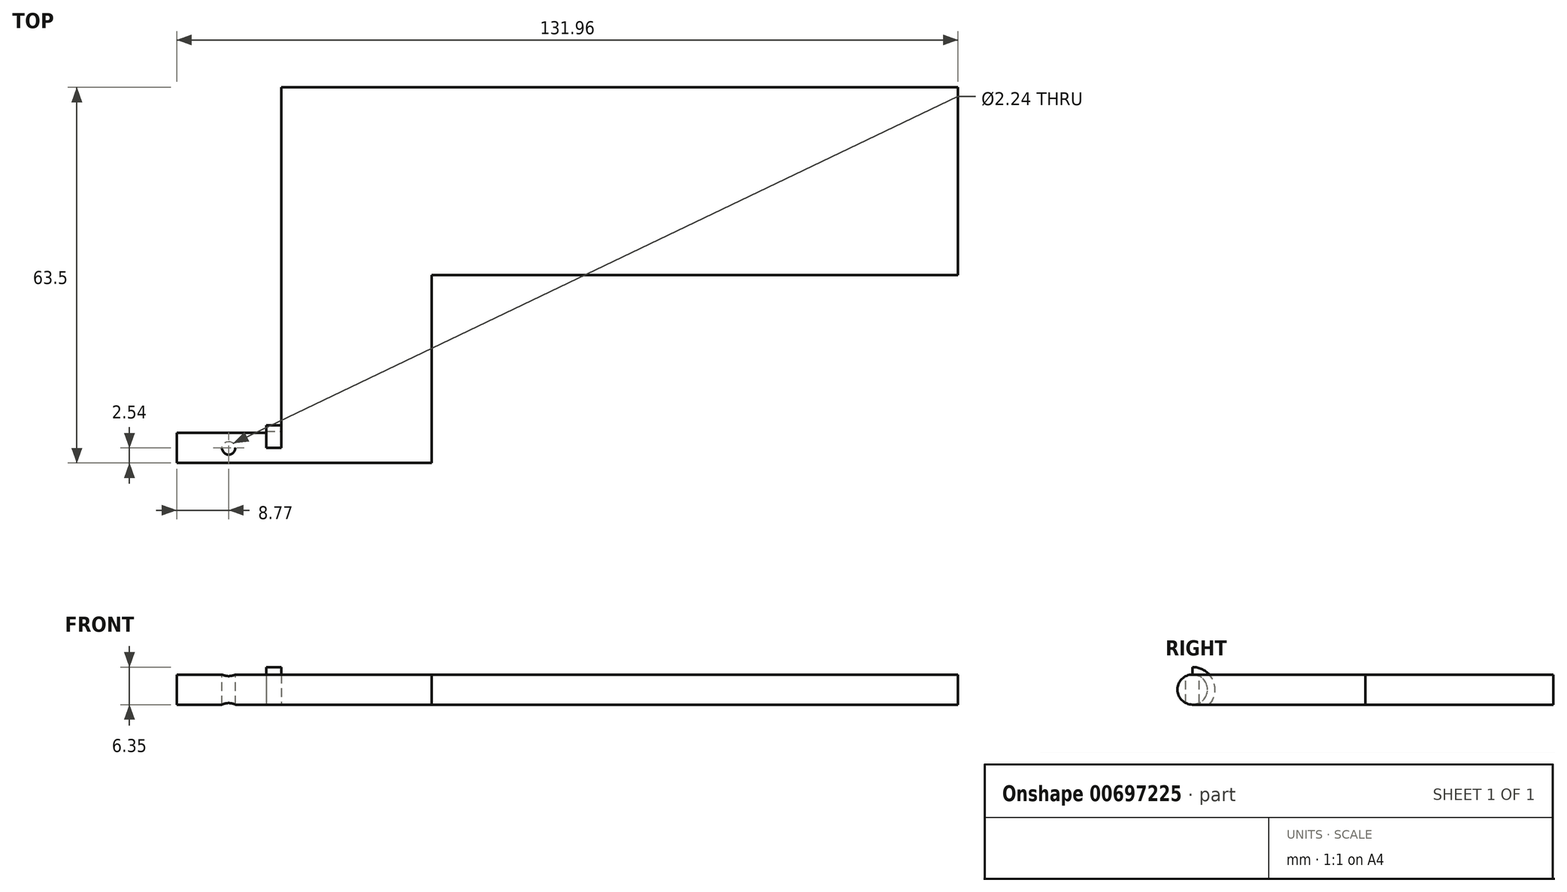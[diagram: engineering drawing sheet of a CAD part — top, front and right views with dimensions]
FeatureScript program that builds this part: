
annotation { "Feature Type Name" : "Feature", "Feature Type Description" : "" }
export const myFeature = defineFeature(function(context is Context, id is Id, definition is map)
    precondition{}
    {
        {
            var Q0;
            Q0=qCreatedBy(makeId("Top.planeOp"),FACE);
            var sketch = newSketch(context, id + "F0", { "sketchPlane" : qUnion([Q0])});
            skLineSegment(sketch, "E0", {"start": v(0, 0) * mm, "end": v(0, 63.5) * mm});
            skLineSegment(sketch, "E1", {"start": v(0, 63.5) * mm, "end": v(114.3, 63.5) * mm});
            skLineSegment(sketch, "E2", {"start": v(114.3, 63.5) * mm, "end": v(114.3, 0) * mm});
            skLineSegment(sketch, "E3", {"start": v(114.3, 0) * mm, "end": v(0, 0) * mm});
            skLineSegment(sketch, "E4", {"start": v(25.4, 0) * mm, "end": v(25.4, 31.75) * mm});
            skLineSegment(sketch, "E5", {"start": v(25.4, 31.75) * mm, "end": v(88.9, 31.75) * mm});
            skLineSegment(sketch, "E6", {"start": v(88.9, 31.75) * mm, "end": v(88.9, 0) * mm});
            skLineSegment(sketch, "E7", {"start": v(88.9, 0) * mm, "end": v(25.4, 0) * mm});
            skLineSegment(sketch, "E8.bottom", {"start": v(0, 0) * mm, "end": v(-17.66, 0) * mm});
            skLineSegment(sketch, "E8.top", {"start": v(0, 5.08) * mm, "end": v(-17.66, 5.08) * mm});
            skLineSegment(sketch, "E8.left", {"start": v(0, 0) * mm, "end": v(0, 5.08) * mm});
            skLineSegment(sketch, "E8.right", {"start": v(-17.66, 0) * mm, "end": v(-17.66, 5.08) * mm});
            skLineSegment(sketch, "E9", {"start": v(0, 5.08) * mm, "end": v(0, 28.75) * mm});
            skLineSegment(sketch, "E10", {"start": v(114.3, 63.5) * mm, "end": v(114.3, 31.75) * mm});
            skLineSegment(sketch, "E11", {"start": v(114.3, 31.75) * mm, "end": v(88.9, 31.75) * mm});
            skSolve(sketch);
        }
        {
            var Q0;
            {var subQ5=sQuery(id+"F0.wireOp",EDGE,"E8.right");Q0=makeQuery(id+"F0.imprint","IMPRINT",FACE,{"disambiguationData":[TD([[makeQuery(id+"F0.imprint","IMPRINT",EDGE,{"derivedFrom":subQ5}),-1.0]])]});}
            var Q1;
            {var subQ5=sQuery(id+"F0.wireOp",EDGE,"E8.left");Q1=makeQuery(id+"F0.imprint","IMPRINT",FACE,{"disambiguationData":[TD([[makeQuery(id+"F0.imprint","IMPRINT",EDGE,{"derivedFrom":subQ5}),1.0]])]});}
            var Q2;
            {var subQ4=sQuery(id+"F0.wireOp",EDGE,"E1");Q2=makeQuery(id+"F0.imprint","IMPRINT",FACE,{"disambiguationData":[TD([[makeQuery(id+"F0.imprint","IMPRINT",EDGE,{"derivedFrom":subQ4}),-1.0]])]});}
            extrude(context, id + "F1", {"entities" : qUnion([Q0, Q1, Q2]), "depth" : 5.08 * mm, "offsetDistance" : 25.4 * mm});
        }
        {
            var Q0;
            Q0=makeQuery(id+"F1.opExtrude","CAP_EDGE",EDGE,{"disambiguationData":[OSD([sQuery(id+"F0.wireOp",EDGE,"E3"),sQuery(id+"F0.wireOp",EDGE,"E8.bottom")])],"isStart":false});
            var Q1;
            Q1=makeQuery(id+"F1.opExtrude","CAP_EDGE",EDGE,{"disambiguationData":[OSD([sQuery(id+"F0.wireOp",EDGE,"E8.top")])],"isStart":false});
            var Q2;
            Q2=makeQuery(id+"F1.opExtrude","CAP_EDGE",EDGE,{"disambiguationData":[OSD([sQuery(id+"F0.wireOp",EDGE,"E3"),sQuery(id+"F0.wireOp",EDGE,"E8.bottom")])],"isStart":true});
            var Q3;
            Q3=makeQuery(id+"F1.opExtrude","CAP_EDGE",EDGE,{"disambiguationData":[OSD([sQuery(id+"F0.wireOp",EDGE,"E8.top")])],"isStart":true});
            fillet(context, id + "F2", {"entities" : qUnion([Q0, Q1, Q2, Q3]), "radius" : 2.54 * mm, "tangentPropagation" : true, "allowEdgeOverflow" : false});
        }
        {
            var Q0;
            Q0=makeQuery(id+"F1.opExtrude","CAP_FACE",FACE,{"disambiguationData":[OSD([sQuery(id+"F0.wireOp",EDGE,"E0"),sQuery(id+"F0.wireOp",EDGE,"E1"),sQuery(id+"F0.wireOp",EDGE,"E3"),sQuery(id+"F0.wireOp",EDGE,"E4"),sQuery(id+"F0.wireOp",EDGE,"E5"),sQuery(id+"F0.wireOp",EDGE,"E8.bottom"),sQuery(id+"F0.wireOp",EDGE,"E8.top"),sQuery(id+"F0.wireOp",EDGE,"E8.right"),sQuery(id+"F0.wireOp",EDGE,"E9"),sQuery(id+"F0.wireOp",EDGE,"E10"),sQuery(id+"F0.wireOp",EDGE,"E11")])],"isStart":false});
            var sketch = newSketch(context, id + "F3", { "sketchPlane" : qUnion([Q0])});
            skLineSegment(sketch, "E12", {"start": v(69.85, 31.75) * mm, "end": v(69.85, 0) * mm});
            skLineSegment(sketch, "E13", {"start": v(69.85, 0) * mm, "end": v(-22.45, 0) * mm});
            skLineSegment(sketch, "E14", {"start": v(-22.45, 0) * mm, "end": v(-22.45, 2.54) * mm});
            skLineSegment(sketch, "E15", {"start": v(-22.45, 2.54) * mm, "end": v(25.4, 2.54) * mm});
            skCircle(sketch, "E16", {"center": v(-8.9, 2.54) * mm, "radius": 1.12 * mm});
            skLineSegment(sketch, "E17", {"start": v(57.15, 63.5) * mm, "end": v(57.15, 0) * mm});
            skSolve(sketch);
        }
        {
            var Q0;
            Q0 = qSketchRegion(id + "F3", true);
            extrude(context, id + "F4", {"entities" : qUnion([Q0]), "operationType" : NewBodyOperationType.REMOVE, "endBound" : BoundingType.THROUGH_ALL, "oppositeDirection" : true, "depth" : 25.4 * mm, "offsetDistance" : 25.4 * mm});
        }
        {
            var Q0;
            Q0=makeQuery(id+"F1.opExtrude","SWEPT_FACE",FACE,{"disambiguationData":[OSD([sQuery(id+"F0.wireOp",EDGE,"E0"),sQuery(id+"F0.wireOp",EDGE,"E9")])]});
            var sketch = newSketch(context, id + "F5", { "sketchPlane" : qUnion([Q0])});
            skCircle(sketch, "E18", {"center": v(-2.54, 2.54) * mm, "radius": 3.81 * mm});
            skLineSegment(sketch, "E19", {"start": v(-2.54, 2.54) * mm, "end": v(-2.54, 6.35) * mm});
            skLineSegment(sketch, "E20", {"start": v(-2.54, 2.54) * mm, "end": v(-6.35, 2.54) * mm});
            skLineSegment(sketch, "E21", {"start": v(-5.38, 0) * mm, "end": v(-2.54, 0) * mm});
            skLineSegment(sketch, "E22", {"start": v(-2.54, 0) * mm, "end": v(-2.54, 2.54) * mm});
            skSolve(sketch);
        }
        {
            var Q0;
            {var subQ1=sQuery(id+"F0.wireOp",EDGE,"E9");var subQ2=sQuery(id+"F0.wireOp",EDGE,"E0");var subQ7=makeQuery(id+"F2.opFillet","BLEND_EDGE",EDGE,{"blendedFrom":[makeQuery(id+"F1.opExtrude","CAP_EDGE",EDGE,{"disambiguationData":[OSD([sQuery(id+"F0.wireOp",EDGE,"E8.top")])],"isStart":true}),makeQuery(id+"F1.opExtrude","SWEPT_FACE",FACE,{"disambiguationData":[OSD([subQ2,subQ1])]})],"blendedInto":[makeQuery(id+"F1.opExtrude","SWEPT_FACE",FACE,{"disambiguationData":[OSD([subQ2,subQ1])]})]});Q0=makeQuery(id+"F5.imprint","IMPRINT",FACE,{"disambiguationData":[TD([[makeQuery(id+"F5.imprint","IMPRINT",EDGE,{"derivedFrom":subQ7}),-1.0]])]});}
            var Q1;
            {var subQ0=sQuery(id+"F5.wireOp",EDGE,"E20");var subQ1=sQuery(id+"F5.wireOp",EDGE,"E18");var subQ2=makeQuery(id+"F5.imprint","INTERSECT",VERTEX,{"derivedFrom":[subQ1,subQ0]});Q1=makeQuery(id+"F5.imprint","IMPRINT",FACE,{"disambiguationData":[TD([[makeQuery(id+"F5.imprint","IMPRINT",EDGE,{"disambiguationData":[TD([[subQ2,1.0]])],"derivedFrom":subQ1}),1.0]])]});}
            var Q2;
            {var subQ0=sQuery(id+"F5.wireOp",EDGE,"E19");var subQ1=sQuery(id+"F5.wireOp",EDGE,"E18");var subQ2=makeQuery(id+"F5.imprint","INTERSECT",VERTEX,{"derivedFrom":[subQ1,subQ0]});Q2=makeQuery(id+"F5.imprint","IMPRINT",FACE,{"disambiguationData":[TD([[makeQuery(id+"F5.imprint","IMPRINT",EDGE,{"disambiguationData":[TD([[subQ2,-1.0]])],"derivedFrom":subQ1}),1.0]])]});}
            var Q3;
            {var subQ3=sQuery(id+"F5.wireOp",EDGE,"E21");Q3=makeQuery(id+"F5.imprint","IMPRINT",FACE,{"disambiguationData":[TD([[makeQuery(id+"F5.imprint","IMPRINT",EDGE,{"derivedFrom":subQ3}),-1.0]])]});}
            extrude(context, id + "F6", {"entities" : qUnion([Q0, Q1, Q2, Q3]), "operationType" : NewBodyOperationType.ADD, "depth" : 2.54 * mm, "offsetDistance" : 25.4 * mm});
        }
    });
